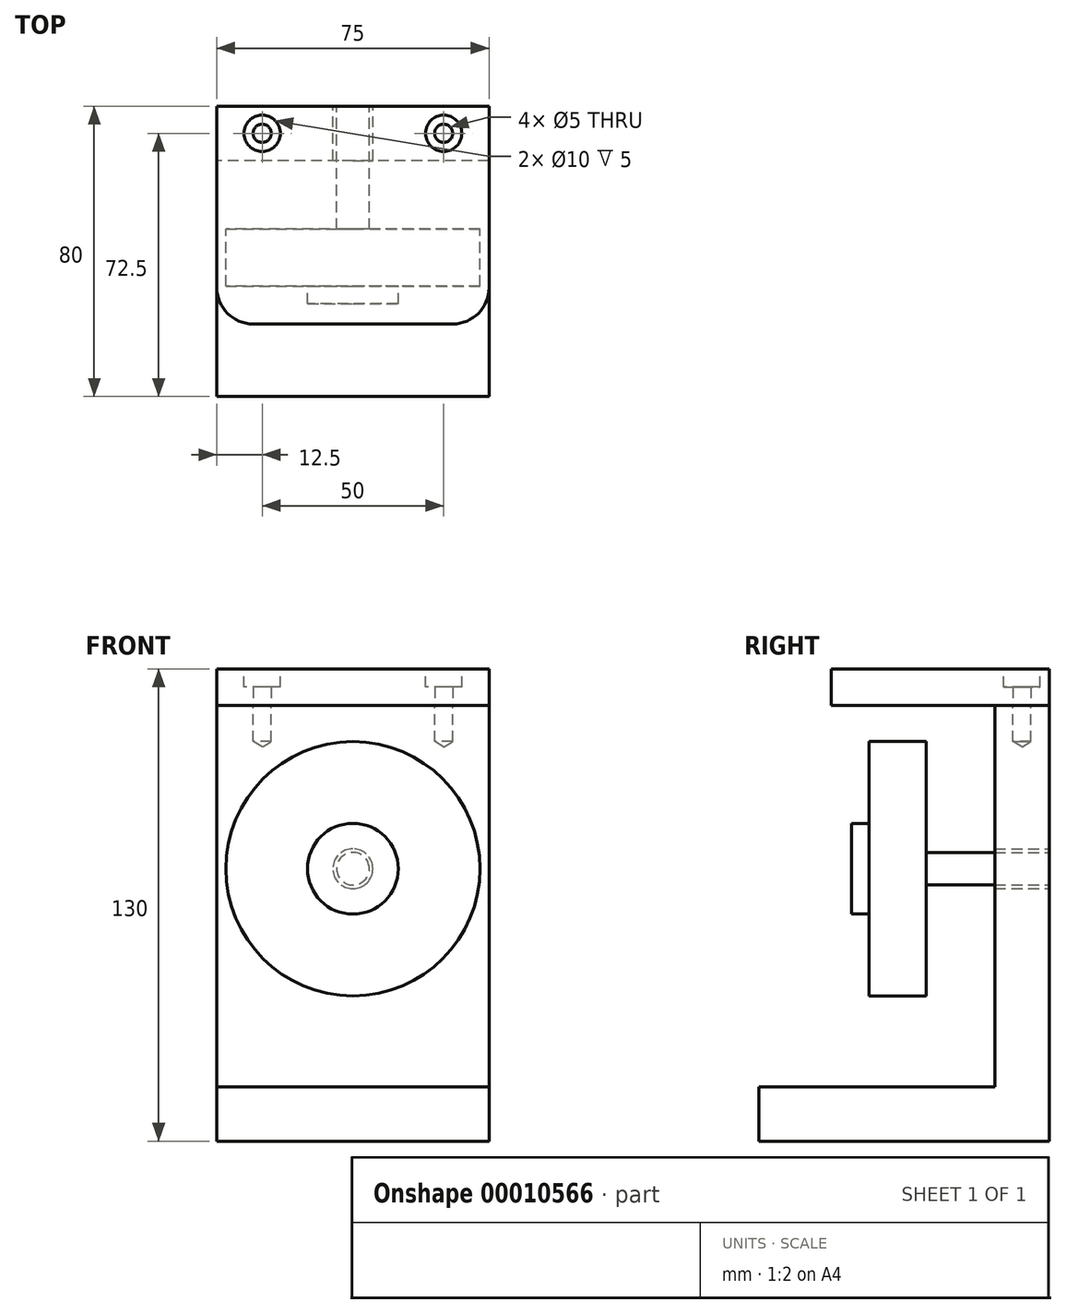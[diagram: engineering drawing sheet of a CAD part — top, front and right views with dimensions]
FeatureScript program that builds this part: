
annotation { "Feature Type Name" : "Feature", "Feature Type Description" : "" }
export const myFeature = defineFeature(function(context is Context, id is Id, definition is map)
    precondition{}
    {
        {
            var Q0;
            Q0=qCreatedBy(makeId("Right.planeOp"),FACE);
            var sketch = newSketch(context, id + "F0", { "sketchPlane" : qUnion([Q0])});
            skLineSegment(sketch, "E0", {"start": v(-80, 0) * mm, "end": v(0, 0) * mm});
            skLineSegment(sketch, "E1", {"start": v(0, 0) * mm, "end": v(0, 120) * mm});
            skLineSegment(sketch, "E2.0", {"start": v(-15, 15) * mm, "end": v(-15, 120) * mm});
            skLineSegment(sketch, "E2.1", {"start": v(-80, 15) * mm, "end": v(-15, 15) * mm});
            skLineSegment(sketch, "E3", {"start": v(-15, 120) * mm, "end": v(0, 120) * mm});
            skLineSegment(sketch, "E4", {"start": v(-80, 0) * mm, "end": v(-80, 15) * mm});
            skSolve(sketch);
        }
        {
            var Q0;
            Q0=makeQuery(id+"F0.imprint","IMPRINT",FACE,{"disambiguationData":[TD([[makeQuery(id+"F0.imprint","IMPRINT",EDGE,{"derivedFrom":sQuery(id+"F0.wireOp",EDGE,"E0")}),1.0]])]});
            extrude(context, id + "F1", {"entities" : qUnion([Q0]), "endBound" : BoundingType.SYMMETRIC, "depth" : 75 * mm});
        }
        {
            var Q0;
            Q0=makeQuery(id+"F1.opExtrude","SWEPT_FACE",FACE,{"disambiguationData":[OSD([sQuery(id+"F0.wireOp",EDGE,"E1")])]});
            var sketch = newSketch(context, id + "F2", { "sketchPlane" : qUnion([Q0])});
            skPoint(sketch, "E5", {"position": v(0, 75) * mm});
            skSolve(sketch);
        }
        {
            var Q0;
            Q0=sQuery(id+"F2.wireOp",VERTEX,"E5");
            var Q1;
            Q1=makeQuery(id+"F1.opExtrude","SWEPT_BODY",BODY,{"disambiguationData":[OSD([sQuery(id+"F0.wireOp",EDGE,"E0"),sQuery(id+"F0.wireOp",EDGE,"E1"),sQuery(id+"F0.wireOp",EDGE,"E2.0"),sQuery(id+"F0.wireOp",EDGE,"E2.1"),sQuery(id+"F0.wireOp",EDGE,"E3"),sQuery(id+"F0.wireOp",EDGE,"E4")])]});
            hole(context, id + "F3", {"style" : HoleStyle.SIMPLE, "holeDiameter" : 11 * mm, "endStyle" : HoleEndStyle.THROUGH, "locations" : qUnion([Q0]), "scope" : qUnion([Q1])});
        }
        {
            var Q0;
            Q0=makeQuery(id+"F1.opExtrude","SWEPT_FACE",FACE,{"disambiguationData":[OSD([sQuery(id+"F0.wireOp",EDGE,"E3")])]});
            var sketch = newSketch(context, id + "F4", { "sketchPlane" : qUnion([Q0])});
            skPoint(sketch, "E6", {"position": v(-25, -7.5) * mm});
            skLineSegment(sketch, "E7", {"start": v(0, 0) * mm, "end": v(0, -15) * mm, "construction": true});
            skLineSegment(sketch, "E8", {"start": v(-37.5, -7.5) * mm, "end": v(37.5, -7.5) * mm, "construction": true});
            skPoint(sketch, "E9", {"position": v(25, -7.5) * mm});
            skSolve(sketch);
        }
        {
            var Q0;
            Q0=sQuery(id+"F4.wireOp",VERTEX,"E6");
            var Q1;
            Q1=sQuery(id+"F4.wireOp",VERTEX,"E9");
            var Q2;
            Q2=makeQuery(id+"F1.opExtrude","SWEPT_BODY",BODY,{"disambiguationData":[OSD([sQuery(id+"F0.wireOp",EDGE,"E0"),sQuery(id+"F0.wireOp",EDGE,"E1"),sQuery(id+"F0.wireOp",EDGE,"E2.0"),sQuery(id+"F0.wireOp",EDGE,"E2.1"),sQuery(id+"F0.wireOp",EDGE,"E3"),sQuery(id+"F0.wireOp",EDGE,"E4")])]});
            hole(context, id + "F5", {"style" : HoleStyle.SIMPLE, "holeDiameter" : 5 * mm, "endStyle" : HoleEndStyle.BLIND, "holeDepth" : 10 * mm, "locations" : qUnion([Q0, Q1]), "scope" : qUnion([Q2])});
        }
        {
            var Q0;
            Q0=makeQuery(id+"F1.opExtrude","SWEPT_FACE",FACE,{"disambiguationData":[OSD([sQuery(id+"F0.wireOp",EDGE,"E3")])]});
            var sketch = newSketch(context, id + "F6", { "sketchPlane" : qUnion([Q0])});
            skLineSegment(sketch, "E10.bottom", {"start": v(-37.5, 0) * mm, "end": v(37.5, 0) * mm});
            skLineSegment(sketch, "E10.top", {"start": v(-37.5, -60) * mm, "end": v(37.5, -60) * mm});
            skLineSegment(sketch, "E10.left", {"start": v(-37.5, 0) * mm, "end": v(-37.5, -60) * mm});
            skLineSegment(sketch, "E10.right", {"start": v(37.5, 0) * mm, "end": v(37.5, -60) * mm});
            skSolve(sketch);
        }
        {
            var Q0;
            {var subQ2=sQuery(id+"F6.wireOp",EDGE,"E10.top");Q0=makeQuery(id+"F6.imprint","IMPRINT",FACE,{"disambiguationData":[TD([[makeQuery(id+"F6.imprint","IMPRINT",EDGE,{"derivedFrom":subQ2}),1.0]])]});}
            var Q1;
            Q1=makeQuery(id+"F6.imprint","IMPRINT",FACE,{"disambiguationData":[TD([[makeQuery(id+"F6.imprint","IMPRINT",EDGE,{"derivedFrom":makeQuery(id+"F5.hole-1.boolean.opBoolean","COPY",EDGE,{"derivedFrom":makeQuery(id+"F5.hole-1.opRevolve","SWEPT_EDGE",EDGE,{"disambiguationData":[OSD([sQuery(id+"F5.hole-1.sketch.wireOp",EDGE,"core_line_2"),sQuery(id+"F5.hole-1.sketch.wireOp",EDGE,"core_line_3")])]})})}),1.0]])]});
            var Q2;
            Q2=makeQuery(id+"F6.imprint","IMPRINT",FACE,{"disambiguationData":[TD([[makeQuery(id+"F6.imprint","IMPRINT",EDGE,{"derivedFrom":makeQuery(id+"F5.hole-0.boolean.opBoolean","COPY",EDGE,{"derivedFrom":makeQuery(id+"F5.hole-0.opRevolve","SWEPT_EDGE",EDGE,{"disambiguationData":[OSD([sQuery(id+"F5.hole-0.sketch.wireOp",EDGE,"core_line_2"),sQuery(id+"F5.hole-0.sketch.wireOp",EDGE,"core_line_3")])]})})}),1.0]])]});
            var Q3;
            {var subQ2=sQuery(id+"F6.wireOp",EDGE,"E10.bottom");Q3=makeQuery(id+"F6.imprint","IMPRINT",FACE,{"disambiguationData":[TD([[makeQuery(id+"F6.imprint","IMPRINT",EDGE,{"derivedFrom":subQ2}),1.0]])]});}
            extrude(context, id + "F7", {"entities" : qUnion([Q0, Q1, Q2, Q3]), "depth" : 10 * mm});
        }
        {
            var Q0;
            Q0=makeQuery(id+"F7.opExtrude","CAP_FACE",FACE,{"disambiguationData":[OSD([sQuery(id+"F6.wireOp",EDGE,"E10.bottom"),sQuery(id+"F6.wireOp",EDGE,"E10.top"),sQuery(id+"F6.wireOp",EDGE,"E10.left"),sQuery(id+"F6.wireOp",EDGE,"E10.right")])],"isStart":false});
            var sketch = newSketch(context, id + "F8", { "sketchPlane" : qUnion([Q0])});
            skLineSegment(sketch, "E11.0", {"start": v(-37.5, -7.5) * mm, "end": v(37.5, -7.5) * mm, "construction": true});
            skLineSegment(sketch, "E12.0", {"start": v(0, 0) * mm, "end": v(0, -15) * mm, "construction": true});
            skPoint(sketch, "E13.0", {"position": v(-25, -7.5) * mm});
            skPoint(sketch, "E14.0", {"position": v(25, -7.5) * mm});
            skSolve(sketch);
        }
        {
            var Q0;
            Q0=sQuery(id+"F8.wireOp",VERTEX,"E13.0");
            var Q1;
            Q1=sQuery(id+"F8.wireOp",VERTEX,"E14.0");
            var Q2;
            Q2=makeQuery(id+"F7.opExtrude","SWEPT_BODY",BODY,{"disambiguationData":[OSD([sQuery(id+"F6.wireOp",EDGE,"E10.bottom"),sQuery(id+"F6.wireOp",EDGE,"E10.top"),sQuery(id+"F6.wireOp",EDGE,"E10.left"),sQuery(id+"F6.wireOp",EDGE,"E10.right")])]});
            hole(context, id + "F9", {"style" : HoleStyle.C_BORE, "holeDiameter" : 5 * mm, "cBoreDiameter" : 10 * mm, "cBoreDepth" : 5 * mm, "endStyle" : HoleEndStyle.THROUGH, "locations" : qUnion([Q0, Q1]), "scope" : qUnion([Q2])});
        }
        {
            var Q0;
            Q0=makeQuery(id+"F7.opExtrude","SWEPT_EDGE",EDGE,{"disambiguationData":[OSD([sQuery(id+"F6.wireOp",EDGE,"E10.top"),sQuery(id+"F6.wireOp",EDGE,"E10.right")])]});
            var Q1;
            Q1=makeQuery(id+"F7.opExtrude","SWEPT_EDGE",EDGE,{"disambiguationData":[OSD([sQuery(id+"F6.wireOp",EDGE,"E10.top"),sQuery(id+"F6.wireOp",EDGE,"E10.left")])]});
            fillet(context, id + "F10", {"entities" : qUnion([Q0, Q1]), "radius" : 10 * mm, "tangentPropagation" : true, "allowEdgeOverflow" : false});
        }
        {
            var Q0;
            Q0=qCreatedBy(makeId("Right.planeOp"),FACE);
            var sketch = newSketch(context, id + "F11", { "sketchPlane" : qUnion([Q0])});
            skLineSegment(sketch, "E15", {"start": v(5.44, 75) * mm, "end": v(-71.98, 75) * mm, "construction": true});
            skLineSegment(sketch, "E16.bottom", {"start": v(0, 75) * mm, "end": v(-33.87, 75) * mm});
            skLineSegment(sketch, "E16.top", {"start": v(0, 79.5) * mm, "end": v(-33.87, 79.5) * mm});
            skLineSegment(sketch, "E16.left", {"start": v(0, 75) * mm, "end": v(0, 79.5) * mm});
            skLineSegment(sketch, "E16.right", {"start": v(-33.87, 75) * mm, "end": v(-33.87, 79.5) * mm});
            skLineSegment(sketch, "E17.bottom", {"start": v(-33.87, 75) * mm, "end": v(-49.6, 75) * mm});
            skLineSegment(sketch, "E17.top", {"start": v(-33.87, 110) * mm, "end": v(-49.6, 110) * mm});
            skLineSegment(sketch, "E17.left", {"start": v(-33.87, 75) * mm, "end": v(-33.87, 110) * mm});
            skLineSegment(sketch, "E17.right", {"start": v(-49.6, 75) * mm, "end": v(-49.6, 110) * mm});
            skLineSegment(sketch, "E18.bottom", {"start": v(-54.44, 87.5) * mm, "end": v(-45.97, 87.5) * mm});
            skLineSegment(sketch, "E18.top", {"start": v(-54.44, 75) * mm, "end": v(-45.97, 75) * mm});
            skLineSegment(sketch, "E18.left", {"start": v(-54.44, 87.5) * mm, "end": v(-54.44, 75) * mm});
            skLineSegment(sketch, "E18.right", {"start": v(-45.97, 87.5) * mm, "end": v(-45.97, 75) * mm});
            skSolve(sketch);
        }
        {
            var Q0;
            Q0 = qSketchRegion(id + "F11", true);
            var Q1;
            Q1=sQuery(id+"F11.wireOp",EDGE,"E15");
            revolve(context, id + "F12", {"entities" : qUnion([Q0]), "axis" : qUnion([Q1]), "revolveType" : RevolveType.FULL});
        }
    });
